# Revit family: Geberit Duofix element za konzolnu WC šolju, 112 cm, sa Sigma ugradnim vodokotlićem 12 cm, za osobe sa invaliditetom, za oslonce i rukohvate_PRO_100863
name_source: partatom
category: Plumbing Fixtures
revit_build: Autodesk Revit 2018 (Build: 20190510_1515(x64)
units: mm (PartAtom-declared; Revit-internal decimal feet)

## family parameters
Always vertical = Yes
Cut with Voids When Loaded = No
OmniClass Number = 23.45.05.00
OmniClass Title = Sanitary Equipment
Part Type = Normal
Room Calculation Point = Yes
Round Connector Dimension = Use Diameter
Shared = No
Work Plane-Based = No

## types (1)
- 111.375.00.5 Geberit Duofix element za konzolnu WC šolju, 112 cm, sa Sigma ugradnim vodokotlićem 12 cm, za osobe sa invaliditetom, za oslonce i rukohvate
    BIM datoteka, datum izmene = 2021.12.01
    BIM datoteka, proizvođač = Geberit
    BIM datoteka, verzija = GEB MG 1.5
    Broj artikla = 111.375.00.5
    CW Connection = Yes
    D = 170 mm  [stored 0.557743 ft]
    D1 = 60 mm  [stored 0.19685 ft]
    Description = Geberit Duofix element za konzolnu WC šolju, 112 cm, sa Sigma ugradnim vodokotlićem 12 cm, za osobe sa invaliditetom, za oslonce i rukohvate
    EAN code basic data = 4025416753100
    Fabrički podešena količina ispiranja = 6 i 3 l
    GEB_culture = sr-RS
    GEB_generic_description = concealed cistern support frame for toilet
    GEB_generic_manufacturer = generic
    GEB_imperial_engineering = No
    GEB_metric_engineering = Yes
    GEB_pimversion = 22.02.12
    GEB_processing_type = T
    GEB_reference = PRO_100863
    GEB_translations = {"ATT_10673":"EAN code basic data","ATT_10773":"Protočni pritisak","ATT_10811":"Opseg podešavanja manje količine vode za ispiranje","ATT_10832":"Maksimalna temperatura vode","ATT_10866":"Fabrički podešena količina ispiranja","applicationPurposes":"Namene","application_range":"Oblast primene","brandName":"Robna marka","characteristics":"Svojstva","connection_description1":"Opis priključka 1","connection_description2":"Opis priključka 2","GEB_connection_diameter1":"Prečnik priključka 1","GEB_connection_diameter2":"Prečnik priključka 2","connection_type_c01":"Vrsta priključka kod priključka 01","connection_type_c02":"Vrsta priključka kod priključka 02","content_creator":"BIM datoteka, proizvođač","content_date_changed":"BIM datoteka, datum izmene","content_version":"BIM datoteka, verzija","key 1000":"Broj artikla","name":"Naziv","productBrand":"Robna marka proizvoda","scopeOfDelivery":"Obim isporuke","type":"Tip","GEB_cut_length_c01":"Maksimalno skraćenje kod priključka 01","actuator front":"Čeono aktiviranje","actuator top":"Gornje aktiviranje","angle":"ugao","placement finished floor":"Na gornjoj ivici gotovog poda","rod spacing 180mm":"Razmak kačenja 180 mm","rod spacing 230mm":"Razmak kačenja 230 mm","sanitary socket":"Spojnica za prelaz","surface height":"Visina debljine poda","warning":"Upozorenje","ATT_10767":"Izračunati protok","ATT_10847":"Minimalni protočni pritisak za izračunati protok","fixed_material":"Osnovni materijal","fixed_material_01":"Osnovni materijal 01","fixed_material_02":"Osnovni materijal 02","fixed_material_03":"Osnovni materijal 03","fixed_material_04":"Osnovni materijal 04","fixed_material_05":"Osnovni materijal 05"}
    GEB_use_DN = Yes
    H = 1120 mm  [stored 3.67454 ft]
    H1 = 230 mm
    H2 = 330 mm
    H3 = 1000 mm  [stored 3.28084 ft]
    HW Connection = No
    IfcDescription = Geberit Duofix element za konzolnu WC šolju, 112 cm, sa Sigma ugradnim vodokotlićem 12 cm, za osobe sa invaliditetom, za oslonce i rukohvate
    IfcExportAs = IfcSanitaryTerminal
    IfcExportType = CISTERN
    Izračunati protok = 0.1 L/s
    LOD300 = No
    LOD400 = Yes
    Maksimalna temperatura vode = 25 °C
    Manufacturer = Geberit
    Minimalni protočni pritisak za izračunati protok = 0.5 bar
    Model = Sigma 12 cm
    Namene = Za suvu gradnju
Za ugradnju u predzidne konstrukcije delimične ili visine etaže
Za ugradnju u instalacione zidove u visini etaže
Za ugradnju u delimičnoj ili kompletnoj visini Geberit Duofix sistemskih zidova za predzidnu montažu
Pogodno za ugradnju u prostorije za osobe sa invaliditetom
Za konzolne WC šolje sa priključnim dimenzijama prema propisu EN 33:2011
Za konzolne WC šolje velike projektovane dužine do 70 cm
Za pričvršćivanje oslonaca i rukohvata
Za jednokoličinsko, dvokoličinsko ili start/stop ispiranje
Za debljine poda 0–20 cm
    Naziv = Geberit Duofix element za konzolnu WC šolju, 112 cm, sa Sigma ugradnim vodokotlićem 12 cm, za osobe sa invaliditetom, za oslonce i rukohvate
    Obim isporuke = Priključak vode R 1/2", kompatibilan sa MF adapterom, sa integrisanim ugaonim ventilom i ručnim točkićem
Građevinska zaštita za revizioni otvor
2 zaštitna čepa
4 zidna sidra
Priključni set za WC, ø 90 mm
Priključno koleno 90° od PE-HD, ø 90 mm
Spojnica za prelaz od PE-HD, ø 90 / 110 mm
2 navojne šipke M12
Ugradna kutija za otvor prečnika ø 68 mm, za priključak električnog napajanja
Materijal za pričvršćivanje
    Oblast primene = sanitary systems
    Opis priključka 1 = cold water in
    Opis priključka 2 = sanitary out
    Opseg podešavanja manje količine vode za ispiranje = 2-4 l
    Osnovni materijal = Geberit, Plastic, Opaque white
    Osnovni materijal 01 = Geberit, Steel, Paint Finish, Blue
    Osnovni materijal 02 = Geberit, Laminate, Ivory, Matte
    Osnovni materijal 03 = Geberit, Steel, galvanized
    Osnovni materijal 04 = Geberit, PE-HD, Black
    Osnovni materijal 05 = Geberit, Wood
    Prečnik priključka 1 = 15 mm  [stored 0.0492126 ft]
    Prečnik priključka 2 = 90 mm  [stored 0.295276 ft]
    Protočni pritisak = 0.1-10 bar
    Robna marka = Geberit
    Robna marka proizvoda = Duofix
    Spojnica za prelaz = No
    Svojstva = Samonoseći okvir sa završnom obradom pečenim lakom
Pripremljen okvir za podupirače kod WC keramike sa malom oslonom površinom
Ugradna visina WC podesiva u sivoj fazi, 41–46 cm
Potporne noge pocinkovane
Potporne noge, podesive od 0–20 cm
Potporne noge sa zaštitom od klizanja
Ploče stope okretne
Dubina ploče stope odgovara za ugradnju u U-profile UW 50 i UW 75 i Geberit Duofix sistemske šine
Priključno koleno koje se može montirati bez alata na različitim dubinama, opseg podešavanja 45 mm
Učvršćenje priključnog kolena, zvučno izolovano
Ugradni vodokotlić sa aktiviranjem sa prednje strane
Ugradni vodokotlić sa izolacijom protiv kondenzacije
Kod fabričkog podešavanja moguće je automatsko naknadno ispiranje
Radovi na montaži i servisu na ugradnom vodokotliću bez alata
Priključak za vodu, pozadi ili gore na sredini
Građevinska zaštita štiti otvor za servisiranje od vlage i prljavštine
Građevinska zaštita za revizioni otvor koja se može seći prema dužini
Montažna ploča od panela, vodootporno zalepljena
Klasa građevinskih materijala B2 prema standardu DIN 4102-1, odn. D-s2, d0 prema standardu DIN EN 13501-3
Klasa A oslobađanja formaldehida prema standardu EN 1084, odnosno klasa E 1 u skladu sa standardom EN 13936
Opremljen praznom cevi za dovod vode ka priključku Geberit AquaClean uređaja za WC tuš
Sa mogućnošću učvršćenja za priključak električnog napajanja
    Tip = Sigma 12 cm
    Vent Connection = No
    Vrsta priključka kod priključka 01 = Rp½''
    Vrsta priključka kod priključka 02 = DN90/ø90 Spigot
    W = 880 mm
    W1 = 425 mm
    Waste Connection = Yes
    Z2_calculated = 226 mm  [stored 0.74147 ft]
    angle_cw = 90.00°
    button_depth = 115 mm  [stored 0.377297 ft]
    cistern_front_offset = 21 mm  [stored 0.0688976 ft]
    cistern_width = 345 mm  [stored 1.13189 ft]
    connection_bend = Yes
    cw_h = 75 mm  [stored 0.246063 ft]
    cw_orientation = 1
    cw_pos = 163 mm
    frame_btm = 1039 mm
    h1 = 504 mm
    outlet_flow = 0.0 L/s
    rod_width_180 = 180 mm
    rod_width_230 = 230 mm
    supply_connection_warning = Reducer connected to element not required and should not be accounted for in a BOM
    wt_h = 43 mm  [stored 0.141076 ft]

note: [stored X ft] marks values corroborated as IEEE doubles in the binary element streams (Revit-internal decimal feet)

## geometry (parser evidence)
native form markers: Blend x6, Sweep x5
no freeform markers — native parametric forms only
